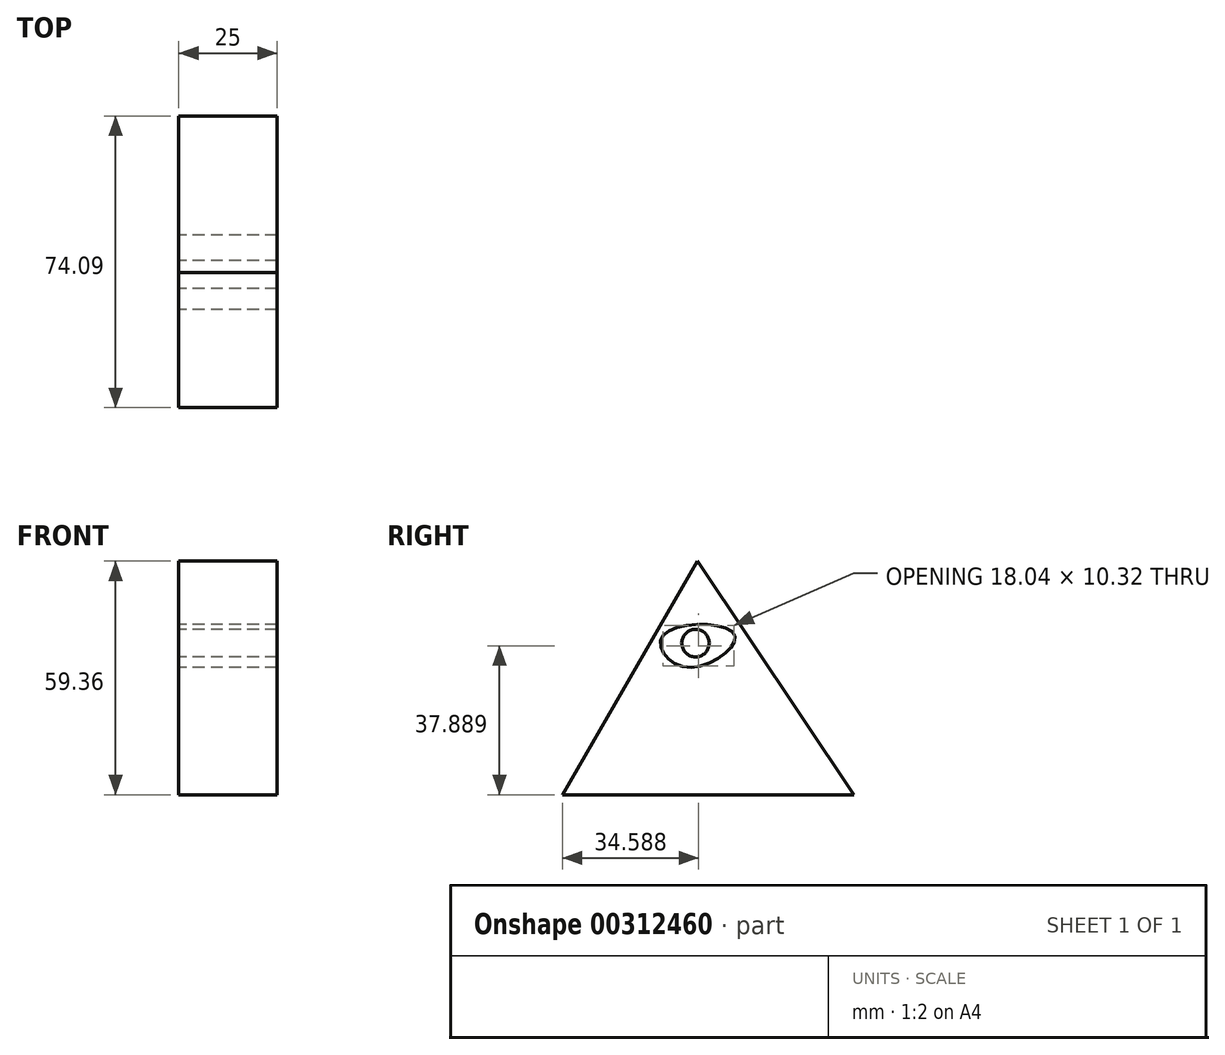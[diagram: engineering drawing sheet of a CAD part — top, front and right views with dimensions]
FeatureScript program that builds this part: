
annotation { "Feature Type Name" : "Feature", "Feature Type Description" : "" }
export const myFeature = defineFeature(function(context is Context, id is Id, definition is map)
    precondition{}
    {
        {
            var Q0;
            Q0=qCreatedBy(makeId("Right.planeOp"),FACE);
            var sketch = newSketch(context, id + "F0", { "sketchPlane" : qUnion([Q0])});
            skLineSegment(sketch, "E0", {"start": v(-36.27, 0) * mm, "end": v(37.82, 0) * mm});
            skLineSegment(sketch, "E1", {"start": v(37.82, 0) * mm, "end": v(-1.94, 59.36) * mm});
            skLineSegment(sketch, "E2", {"start": v(-1.94, 59.36) * mm, "end": v(-36.27, 0) * mm});
            skFitSpline(sketch, "E3", {"points": [v(-10.67, 40.54) * mm, v(7.37, 40.74) * mm, v(-4.66, 32.4) * mm, v(-10.67, 40.54) * mm]});
            skCircle(sketch, "E4", {"center": v(-2.72, 39) * mm, "radius": 4.04 * mm});
            skSolve(sketch);
        }
        {
            var Q0;
            Q0 = qSketchRegion(id + "F0", true);
            extrude(context, id + "F1", {"entities" : qUnion([Q0]), "depth" : 25 * mm});
        }
        {
            var Q0;
            Q0=qCreatedBy(makeId("Right.planeOp"),FACE);
            var sketch = newSketch(context, id + "F2", { "sketchPlane" : qUnion([Q0])});
            skCircle(sketch, "E5", {"center": v(-2.45, 38.55) * mm, "radius": 3.5 * mm});
            skSolve(sketch);
        }
        {
            var Q0;
            Q0 = qSketchRegion(id + "F2", true);
            extrude(context, id + "F3", {"entities" : qUnion([Q0]), "depth" : 25 * mm});
        }
    });
